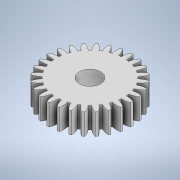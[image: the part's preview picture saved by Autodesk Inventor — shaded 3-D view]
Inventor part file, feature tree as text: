
AUTODESK INVENTOR PART (.ipt)
format: ipt  version: 2022 (Build 260153000, 153)  size: 238,080 bytes
history: native  units: in
note: dims shown in document units (in); Inventor stores cm internally (conversion verified against a paired STEP export)
features: extrude x2, sketch x2, pattern_circular x1
ambient origin geometry x8: Origin, YZ Plane, XZ Plane, XY Plane, X Axis, Y Axis, Z Axis, Center Point
bodies: Solid1 (feature_tree)
feature tree (5):
  extrude  "Extrusion1"  Depth=0.1575in
  pattern_circular  "Circular Pattern1"  [2 undecoded]
  extrude  "Extrusion6"  Depth=0.1969in
  sketch  "Sketch1"  dims[d0=0.6299in d1=0.1575in]
  sketch  "Sketch8"  dims[d2=0.0098in d3=0.0098in d4=0.0236in d7=0.0472in d8=0.1772in d10=0.0787in d11=0.1969in d12=0.0in d13=11.0236in d14=360.0deg d49=0.1969in d50=0.1575in d51=0.5438in d52=0.0in]
note: 2 required parameter values undecoded (feature->parameter linkage not recoverable at this tier; creation-order binding heuristic only, values carry confidence <= 0.55)
